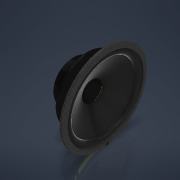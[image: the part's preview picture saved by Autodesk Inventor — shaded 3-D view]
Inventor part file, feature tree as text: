
AUTODESK INVENTOR PART (.ipt)
format: ipt  version: 2022 (Build 260153070, 153G)  size: 673,280 bytes
history: native  units: mm
features: other x11, sketch x6, hole x2, pattern_circular x2, revolve x1, extrude x1
ambient origin geometry x8: Origin, YZ Plane, XZ Plane, XY Plane, X Axis, Y Axis, Z Axis, Center Point
bodies: Body1 (feature_tree)
feature tree (23):
  other  "Твердое тело1"
  revolve  "Вращение1"
  sketch  "Эскиз2"
  sketch  "Эскиз3"
  hole  "Отверстие1"  [1 undecoded]
  pattern_circular  "Круговой массив1"  [2 undecoded]
  hole  "Отверстие2"  [1 undecoded]
  sketch  "Эскиз5"
  extrude  "Выдавливание1"  TaperAngle=360.0deg  [1 undecoded]
  pattern_circular  "Круговой массив2"  Count=6 Angle=360.0deg
  other  "Непосредственное редактирование1"
  other  "Непосредственное редактирование2"
  other  "Непосредственное редактирование3"
  other  "Непосредственное редактирование4"
  other  "Непосредственное редактирование5"
  sketch  "Эскиз1"
  sketch  "Эскиз4"
  sketch  "Эскиз6"
  other  "Масштаб1"
  other  "Масштаб2"
  other  "Масштаб3"
  other  "Масштаб4"
  other  "Масштаб5"
note: 5 required parameter values undecoded (feature->parameter linkage not recoverable at this tier; creation-order binding heuristic only, values carry confidence <= 0.55)
